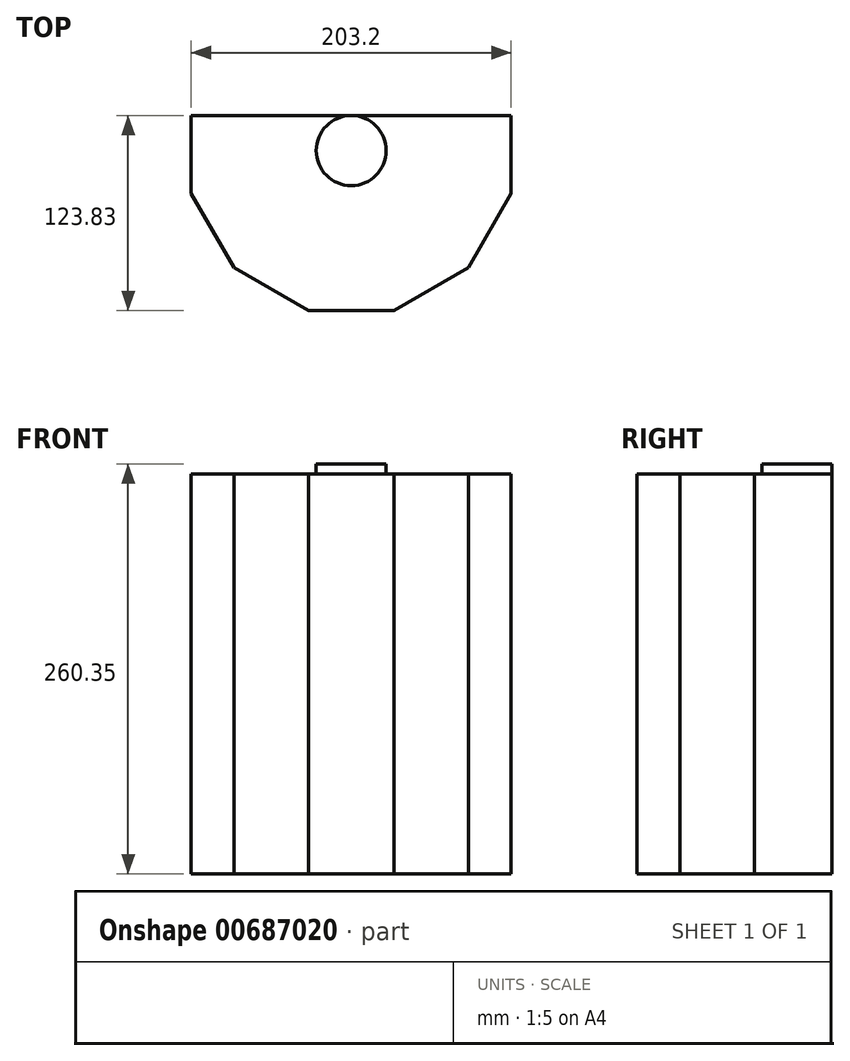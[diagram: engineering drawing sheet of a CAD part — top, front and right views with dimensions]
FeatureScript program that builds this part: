
annotation { "Feature Type Name" : "Feature", "Feature Type Description" : "" }
export const myFeature = defineFeature(function(context is Context, id is Id, definition is map)
    precondition{}
    {
        {
            var Q0;
            Q0=qCreatedBy(makeId("Top.planeOp"),FACE);
            var sketch = newSketch(context, id + "F0", { "sketchPlane" : qUnion([Q0])});
            skCircle(sketch, "E0.cCircle", {"center": v(0, 0) * mm, "radius": 101.6 * mm, "construction": true});
            skLineSegment(sketch, "E0.3", {"start": v(101.6, 22.23) * mm, "end": v(101.6, -27.22) * mm});
            skLineSegment(sketch, "E0.4", {"start": v(101.6, -27.22) * mm, "end": v(74.38, -74.38) * mm});
            skLineSegment(sketch, "E0.5", {"start": v(74.38, -74.38) * mm, "end": v(27.22, -101.6) * mm});
            skLineSegment(sketch, "E0.6", {"start": v(27.22, -101.6) * mm, "end": v(-27.22, -101.6) * mm});
            skLineSegment(sketch, "E0.7", {"start": v(-27.22, -101.6) * mm, "end": v(-74.38, -74.38) * mm});
            skLineSegment(sketch, "E0.8", {"start": v(-74.38, -74.38) * mm, "end": v(-101.6, -27.22) * mm});
            skLineSegment(sketch, "E0.9", {"start": v(-101.6, -27.22) * mm, "end": v(-101.6, 22.22) * mm});
            skPoint(sketch, "E0.0.midPoint", {"position": v(0, 101.6) * mm});
            skPoint(sketch, "E1.orphan", {"position": v(-74.38, 74.38) * mm});
            skPoint(sketch, "E2.orphan", {"position": v(-27.22, 101.6) * mm});
            skPoint(sketch, "E3.orphan", {"position": v(27.22, 101.6) * mm});
            skPoint(sketch, "E4.orphan", {"position": v(74.38, 74.38) * mm});
            skCircle(sketch, "E5", {"center": v(0, 0) * mm, "radius": 22.23 * mm, "construction": true});
            skLineSegment(sketch, "E6", {"start": v(0, 22.23) * mm, "end": v(101.6, 22.23) * mm});
            skLineSegment(sketch, "E7", {"start": v(0, 22.23) * mm, "end": v(-101.6, 22.22) * mm});
            skPoint(sketch, "E8.orphan", {"position": v(-101.6, 27.22) * mm});
            skPoint(sketch, "E9.orphan", {"position": v(101.6, 27.22) * mm});
            skSolve(sketch);
        }
        {
            var Q0;
            Q0 = qSketchRegion(id + "F0", true);
            extrude(context, id + "F1", {"entities" : qUnion([Q0]), "depth" : 254 * mm, "offsetDistance" : 25.4 * mm});
        }
        {
            var Q0;
            Q0=makeQuery(id+"F1.opExtrude","CAP_FACE",FACE,{"disambiguationData":[OSD([sQuery(id+"F0.wireOp",EDGE,"E0.3"),sQuery(id+"F0.wireOp",EDGE,"E0.4"),sQuery(id+"F0.wireOp",EDGE,"E0.5"),sQuery(id+"F0.wireOp",EDGE,"E0.6"),sQuery(id+"F0.wireOp",EDGE,"E0.7"),sQuery(id+"F0.wireOp",EDGE,"E0.8"),sQuery(id+"F0.wireOp",EDGE,"E0.9"),sQuery(id+"F0.wireOp",EDGE,"E6"),sQuery(id+"F0.wireOp",EDGE,"E7")])],"isStart":false});
            var sketch = newSketch(context, id + "F2", { "sketchPlane" : qUnion([Q0])});
            skCircle(sketch, "E10", {"center": v(0, 0) * mm, "radius": 22.23 * mm});
            skSolve(sketch);
        }
        {
            var Q0;
            Q0 = qSketchRegion(id + "F2", true);
            extrude(context, id + "F3", {"entities" : qUnion([Q0]), "operationType" : NewBodyOperationType.ADD, "depth" : 6.35 * mm, "offsetDistance" : 25.4 * mm});
        }
    });
